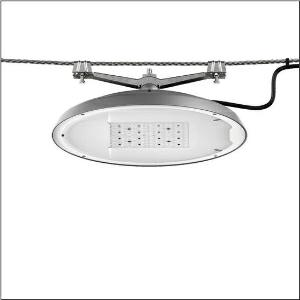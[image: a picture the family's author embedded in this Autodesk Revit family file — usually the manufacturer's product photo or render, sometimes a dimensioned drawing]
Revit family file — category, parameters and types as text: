
# Revit family: dl_r__50_iq_mini___st1_0s_5xa248w41f08le_08ea
name_source: partatom
category: Lighting Fixtures
units: mm (PartAtom-declared; Revit-internal decimal feet)

## family parameters
Cut with Voids When Loaded = No
Host = Face
Light Source = No
Part Type = Normal
Room Calculation Point = No
Round Connector Dimension = Use Diameter
Shared = No

## types (1)
- --- (1 x LED, 10390 lm, 64.1 W, 4000K)
    Apparent Load = 64 VA
    CIE Flux Codes = 37 72 97 100 100
    Color Rendering = 70
    Color Temperature = 4000K
    Default Elevation = 1800 mm
    Description = DL® 50 iQ mini, catenary luminaire, primary light control with lens, of PMMA, primary optical cover: cover, of toughened safety glass, transparent, light distribution: ST1.0s, light emission: direct distribution, primary light characteristic: symmetric, installation type: suspended mounting, LED, High Power LED, rated luminous flux: 10.390lm, luminous efficacy: 162lm/W, light colour: 740, colour temperature: 4000K, control: optimised constant luminous flux control (CLO 2.0), Desk-Remote (wireless, voltage-free reading and setting of iQ features in the workshop via application-optimized NFC function/RFID function), Light-Fading, Smart-Wire, Night-Set, Lumen-Switch, Temp-Guard, Auto-Match, Street-Remote, mains connection: 230..240V, AC, 50/60Hz, start of lifetime: 64W, end of service life: 67W, reduction: 30W, luminaire housing, of diecast aluminium, powder-coated, Siteco® metallic grey (DB 702S), diameter: 500mm, height: 115mm, protection rating (complete): IP66, insulation class (complete): insulation class II (safety insulation), certification: CE, ENEC, VDE, impact resistance: IK08, permissible operating ambient temperature for outdoor applications: -25..+40°C, standard-compliant lighting for roads and squares, packaging unit: 1 piece

Light Distribution: ST1.0s
    Height = 124 mm  [stored 0.406824 ft]
    Lamp = 1 x LED
    Lamp Light Flux = 10390 lm
    Lamp Power = 64.1 W
    Lamp count = 1
    Length = 500 mm
    Luminous efficacy = 162 lm/W
    Manufacturer = Siteco
    ModVariant = No
    Model = 5XA248W41F08LE
    Number of Poles = 1
    OnlyDefault = Yes
    Power Factor = 1
    Product Name = DL® 50 iQ mini | ST1.0s
    Product group = catenary luminaire
    ProductGroupID = 6300
    Protection Class = Protection class II
    Protection Degree = IP 66
    RLX_Detail_Level = 1
    RLX_Emergency_Light_Flux = 0 lm
    RLX_Emergency_Type = 0
    RLX_Emergency_Type_DB = No
    RlxData = <blob elided: 126849 chars, md5=88b206bf>
    Socket = socket
    Standby Power = 0 W
    System Light Flux = 10390 lm
    System Power = 64 W
    Type Comments = factory setting: luminous flux: 100 % | dim-lin: 254 | 672 mA
    Type Image = l_1251783.jpg
    URL = http://relux.com
    VarID = @adj_089857
    Voltage = 0 V
    Weight = 0.00 kg
    Width = 0 mm  [stored 0 ft]

note: [stored X ft] marks values corroborated as IEEE doubles in the binary element streams (Revit-internal decimal feet)

## geometry (parser evidence)
native form markers: Blend x4, Sweep x13
no freeform markers — native parametric forms only
